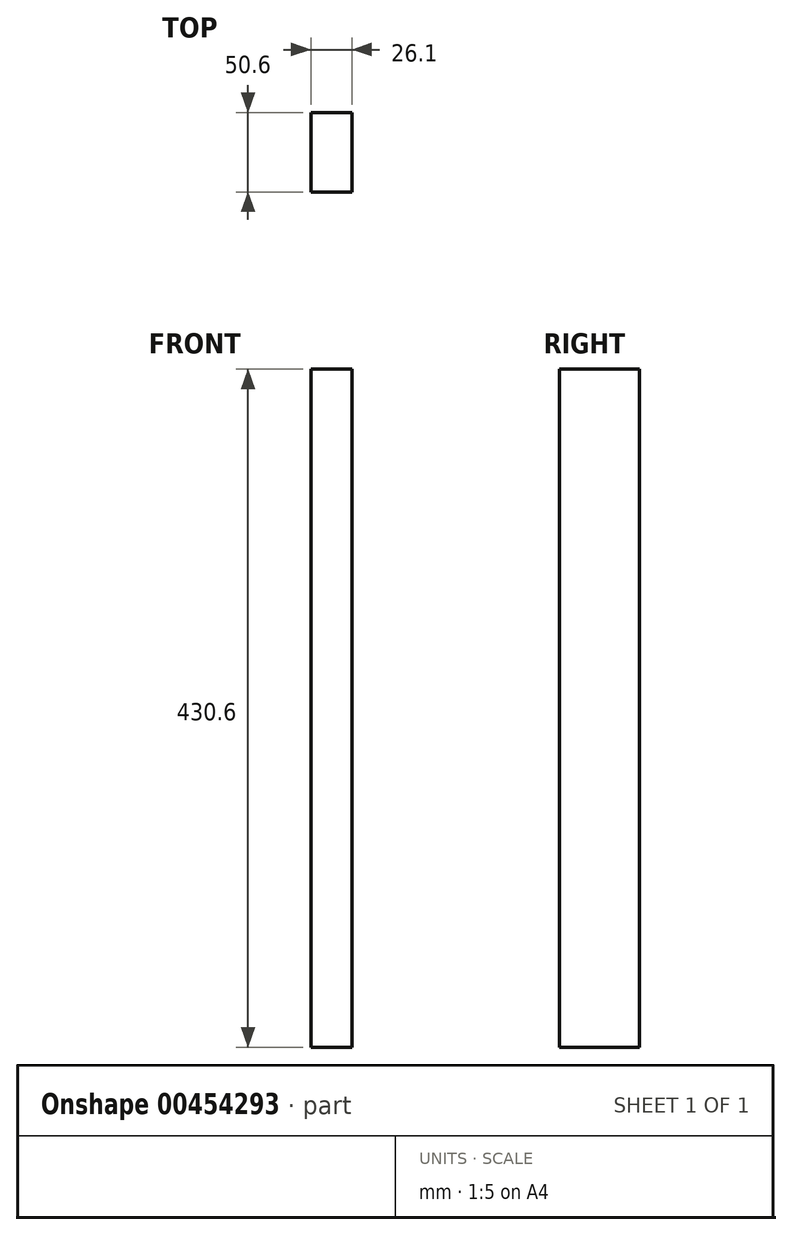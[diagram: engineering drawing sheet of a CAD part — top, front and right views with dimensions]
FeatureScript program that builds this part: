
annotation { "Feature Type Name" : "Feature", "Feature Type Description" : "" }
export const myFeature = defineFeature(function(context is Context, id is Id, definition is map)
    precondition{}
    {
        {
            var Q0;
            Q0=qCreatedBy(makeId("Top.planeOp"),FACE);
            var sketch = newSketch(context, id + "F0", { "sketchPlane" : qUnion([Q0])});
            skLineSegment(sketch, "E0.bottom", {"start": v(13.05, -25.3) * mm, "end": v(-13.05, -25.3) * mm});
            skLineSegment(sketch, "E0.top", {"start": v(13.05, 25.3) * mm, "end": v(-13.05, 25.3) * mm});
            skLineSegment(sketch, "E0.left", {"start": v(13.05, -25.3) * mm, "end": v(13.05, 25.3) * mm});
            skLineSegment(sketch, "E0.right", {"start": v(-13.05, -25.3) * mm, "end": v(-13.05, 25.3) * mm});
            skPoint(sketch, "E0.middle", {"position": v(0, 0) * mm});
            skSolve(sketch);
        }
        {
            var Q0;
            Q0=makeQuery(id+"F0.imprint","IMPRINT",FACE,{"disambiguationData":[TD([[makeQuery(id+"F0.imprint","IMPRINT",EDGE,{"derivedFrom":sQuery(id+"F0.wireOp",EDGE,"E0.bottom")}),-1.0]])]});
            extrude(context, id + "F1", {"entities" : qUnion([Q0]), "oppositeDirection" : true, "depth" : 430.6 * mm});
        }
    });
